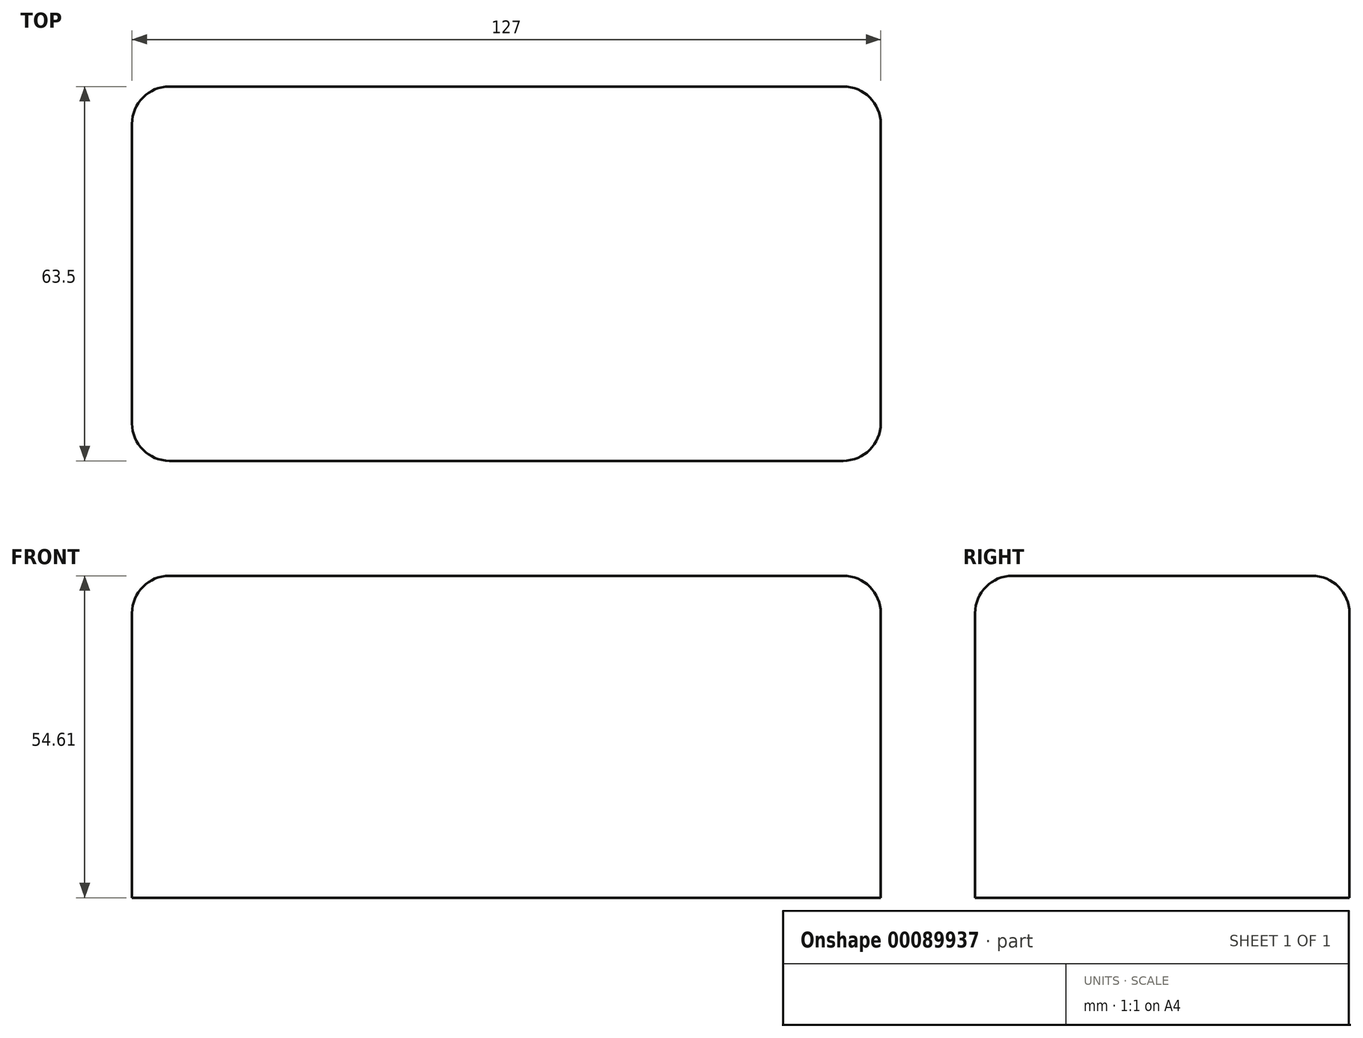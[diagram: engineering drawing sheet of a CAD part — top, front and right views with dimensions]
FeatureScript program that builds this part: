
annotation { "Feature Type Name" : "Feature", "Feature Type Description" : "" }
export const myFeature = defineFeature(function(context is Context, id is Id, definition is map)
    precondition{}
    {
        {
            var Q0;
            Q0=qCreatedBy(makeId("Front.planeOp"),FACE);
            var sketch = newSketch(context, id + "F0", { "sketchPlane" : qUnion([Q0])});
            skLineSegment(sketch, "E0.bottom", {"start": v(0, 0) * mm, "end": v(127, 0) * mm});
            skLineSegment(sketch, "E0.top", {"start": v(0, 54.61) * mm, "end": v(127, 54.61) * mm});
            skLineSegment(sketch, "E0.left", {"start": v(0, 0) * mm, "end": v(0, 54.61) * mm});
            skLineSegment(sketch, "E0.right", {"start": v(127, 0) * mm, "end": v(127, 54.61) * mm});
            skSolve(sketch);
        }
        {
            var Q0;
            Q0=makeQuery(id+"F0.imprint","IMPRINT",FACE,{"disambiguationData":[TD([[makeQuery(id+"F0.imprint","IMPRINT",EDGE,{"derivedFrom":sQuery(id+"F0.wireOp",EDGE,"E0.bottom")}),1.0]])]});
            extrude(context, id + "F1", {"entities" : qUnion([Q0]), "depth" : 63.5 * mm});
        }
        {
            var Q0;
            Q0=makeQuery(id+"F1.opExtrude","CAP_EDGE",EDGE,{"disambiguationData":[OSD([sQuery(id+"F0.wireOp",EDGE,"E0.right")])],"isStart":false});
            var Q1;
            Q1=makeQuery(id+"F1.opExtrude","CAP_EDGE",EDGE,{"disambiguationData":[OSD([sQuery(id+"F0.wireOp",EDGE,"E0.right")])],"isStart":true});
            var Q2;
            Q2=makeQuery(id+"F1.opExtrude","CAP_EDGE",EDGE,{"disambiguationData":[OSD([sQuery(id+"F0.wireOp",EDGE,"E0.left")])],"isStart":false});
            var Q3;
            Q3=makeQuery(id+"F1.opExtrude","CAP_EDGE",EDGE,{"disambiguationData":[OSD([sQuery(id+"F0.wireOp",EDGE,"E0.left")])],"isStart":true});
            fillet(context, id + "F2", {"entities" : qUnion([Q0, Q1, Q2, Q3]), "radius" : 6.35 * mm, "tangentPropagation" : true, "allowEdgeOverflow" : false});
        }
        {
            var Q0;
            Q0=makeQuery(id+"F1.opExtrude","SWEPT_EDGE",EDGE,{"disambiguationData":[OSD([sQuery(id+"F0.wireOp",EDGE,"E0.top"),sQuery(id+"F0.wireOp",EDGE,"E0.left")])]});
            fillet(context, id + "F3", {"entities" : qUnion([Q0]), "radius" : 6.35 * mm, "tangentPropagation" : true, "allowEdgeOverflow" : false});
        }
    });
